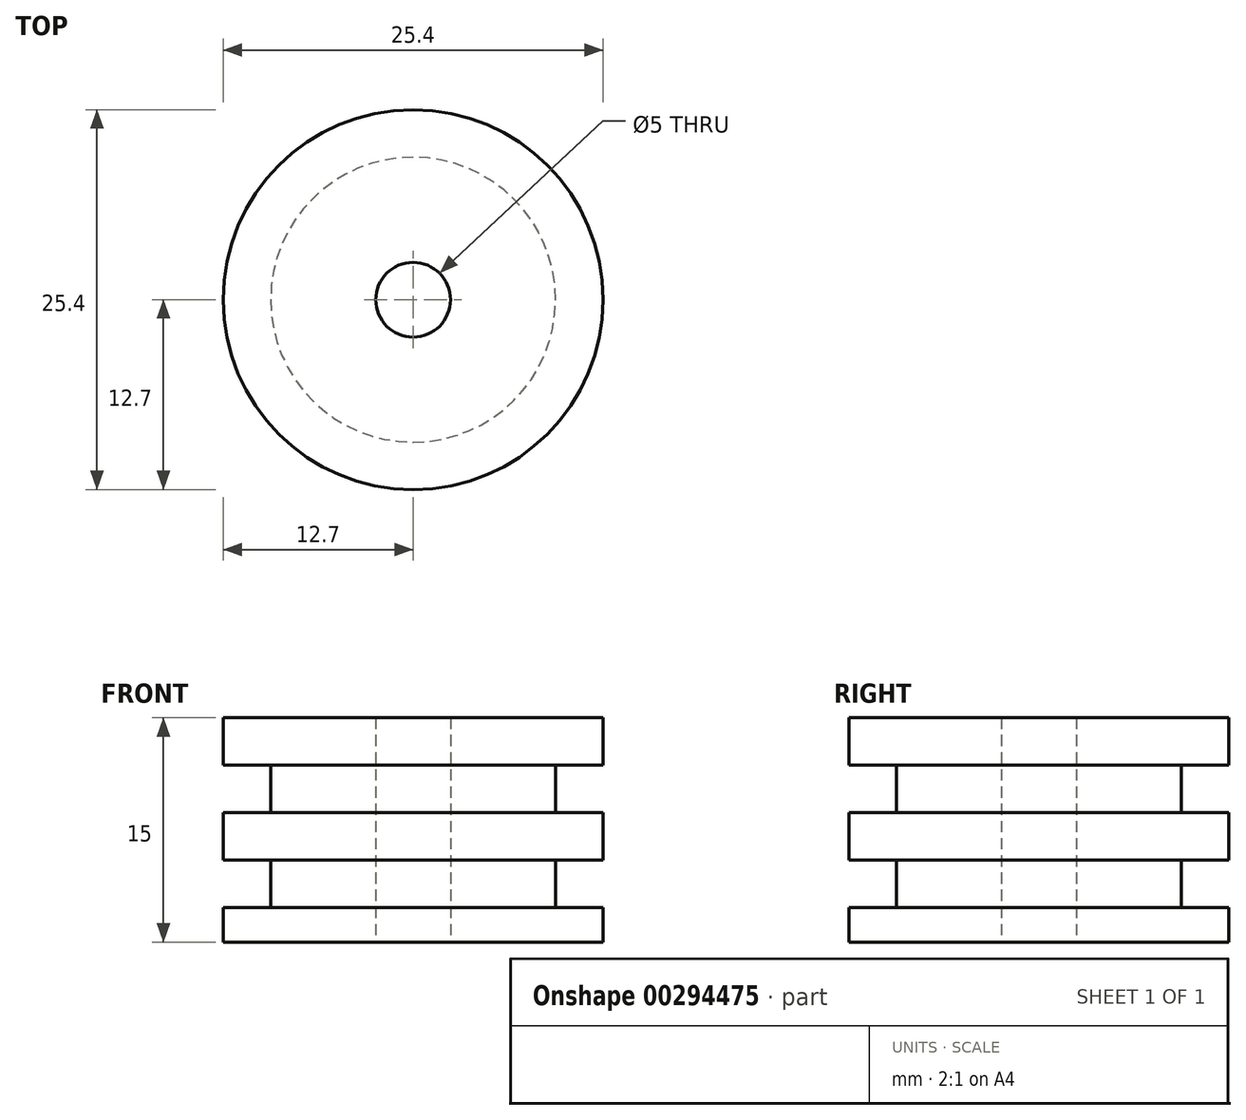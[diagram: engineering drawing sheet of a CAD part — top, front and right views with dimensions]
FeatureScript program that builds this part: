
annotation { "Feature Type Name" : "Feature", "Feature Type Description" : "" }
export const myFeature = defineFeature(function(context is Context, id is Id, definition is map)
    precondition{}
    {
        {
            var Q0;
            Q0=qCreatedBy(makeId("Top.planeOp"),FACE);
            var sketch = newSketch(context, id + "F0", { "sketchPlane" : qUnion([Q0])});
            skCircle(sketch, "E0", {"center": v(0, 0) * mm, "radius": 12.7 * mm});
            skCircle(sketch, "E1", {"center": v(0, 0) * mm, "radius": 9.53 * mm});
            skPoint(sketch, "E2", {"position": v(-12.7, 0) * mm});
            skPoint(sketch, "E3", {"position": v(0, 12.7) * mm});
            skSolve(sketch);
        }
        {
            var Q0;
            Q0=makeQuery(id+"F0.imprint","IMPRINT",FACE,{"disambiguationData":[TD([[makeQuery(id+"F0.imprint","IMPRINT",EDGE,{"derivedFrom":sQuery(id+"F0.wireOp",EDGE,"E0")}),1.0]])]});
            var Q1;
            Q1=makeQuery(id+"F0.imprint","IMPRINT",FACE,{"disambiguationData":[TD([[makeQuery(id+"F0.imprint","IMPRINT",EDGE,{"derivedFrom":sQuery(id+"F0.wireOp",EDGE,"E1")}),1.0]])]});
            extrude(context, id + "F1", {"entities" : qUnion([Q0, Q1]), "depth" : 15 * mm});
        }
        {
            var Q0;
            Q0=qCreatedBy(makeId("Front.planeOp"),FACE);
            var sketch = newSketch(context, id + "F2", { "sketchPlane" : qUnion([Q0])});
            skLineSegment(sketch, "E4", {"start": v(0, -76.4) * mm, "end": v(0, 75.84) * mm, "construction": true});
            skSolve(sketch);
        }
        {
            var Q0;
            Q0=qCreatedBy(makeId("Right.planeOp"),FACE);
            var sketch = newSketch(context, id + "F3", { "sketchPlane" : qUnion([Q0])});
            skLineSegment(sketch, "E5.top", {"start": v(9.53, 2.3) * mm, "end": v(12.7, 2.3) * mm});
            skLineSegment(sketch, "E6", {"start": v(9.53, 5.47) * mm, "end": v(9.53, 2.3) * mm});
            skLineSegment(sketch, "E7", {"start": v(9.53, 5.47) * mm, "end": v(12.7, 5.47) * mm});
            skLineSegment(sketch, "E8", {"start": v(12.7, 5.47) * mm, "end": v(12.7, 2.3) * mm});
            skLineSegment(sketch, "E9", {"start": v(12.7, 8.65) * mm, "end": v(9.53, 8.65) * mm});
            skLineSegment(sketch, "E10", {"start": v(9.53, 8.65) * mm, "end": v(9.53, 11.82) * mm});
            skLineSegment(sketch, "E11", {"start": v(9.53, 11.82) * mm, "end": v(12.7, 11.83) * mm});
            skLineSegment(sketch, "E12", {"start": v(12.7, 11.83) * mm, "end": v(12.7, 8.65) * mm});
            skSolve(sketch);
        }
        {
            var Q0;
            Q0 = qSketchRegion(id + "F3", true);
            var Q1;
            Q1=sQuery(id+"F2.wireOp",EDGE,"E4");
            revolve(context, id + "F4", {"operationType" : NewBodyOperationType.REMOVE, "entities" : qUnion([Q0]), "axis" : qUnion([Q1]), "revolveType" : RevolveType.FULL, "oppositeDirection" : true});
        }
        {
            var Q0;
            Q0=makeQuery(id+"F0.imprint","IMPRINT",FACE,{"disambiguationData":[TD([[makeQuery(id+"F0.imprint","IMPRINT",EDGE,{"derivedFrom":sQuery(id+"F0.wireOp",EDGE,"E0")}),1.0]])]});
            var sketch = newSketch(context, id + "F5", { "sketchPlane" : qUnion([Q0])});
            skCircle(sketch, "E13", {"center": v(0, 0) * mm, "radius": 2.5 * mm});
            skSolve(sketch);
        }
        {
            var Q0;
            Q0=makeQuery(id+"F5.imprint","IMPRINT",FACE,{"disambiguationData":[TD([[makeQuery(id+"F5.imprint","IMPRINT",EDGE,{"derivedFrom":sQuery(id+"F5.wireOp",EDGE,"E13")}),1.0]])]});
            extrude(context, id + "F6", {"entities" : qUnion([Q0]), "operationType" : NewBodyOperationType.REMOVE, "depth" : 25.4 * mm});
        }
    });
